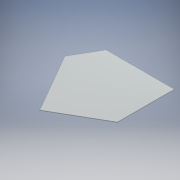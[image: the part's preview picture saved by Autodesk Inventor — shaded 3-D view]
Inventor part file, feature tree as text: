
AUTODESK INVENTOR PART (.ipt)
format: ipt  version: 2016 SP1 (Build 200210100, 210)  size: 125,952 bytes
history: native  units: mm
features: reference x3, extrude x1, sketch x1
ambient origin geometry x8: Origin, YZ Plane, XZ Plane, XY Plane, X Axis, Y Axis, Z Axis, Center Point
bodies: Solid1 (feature_tree)
feature tree (5):
  extrude  "Extrusion1"  [1 undecoded]
  sketch  "Sketch1"  dims[d0=1.5mm d1=0.0mm]
  reference  "Reference1"
  reference  "Reference2"
  reference  "Reference3"
note: 1 required parameter value undecoded (feature->parameter linkage not recoverable at this tier; creation-order binding heuristic only, values carry confidence <= 0.55)
